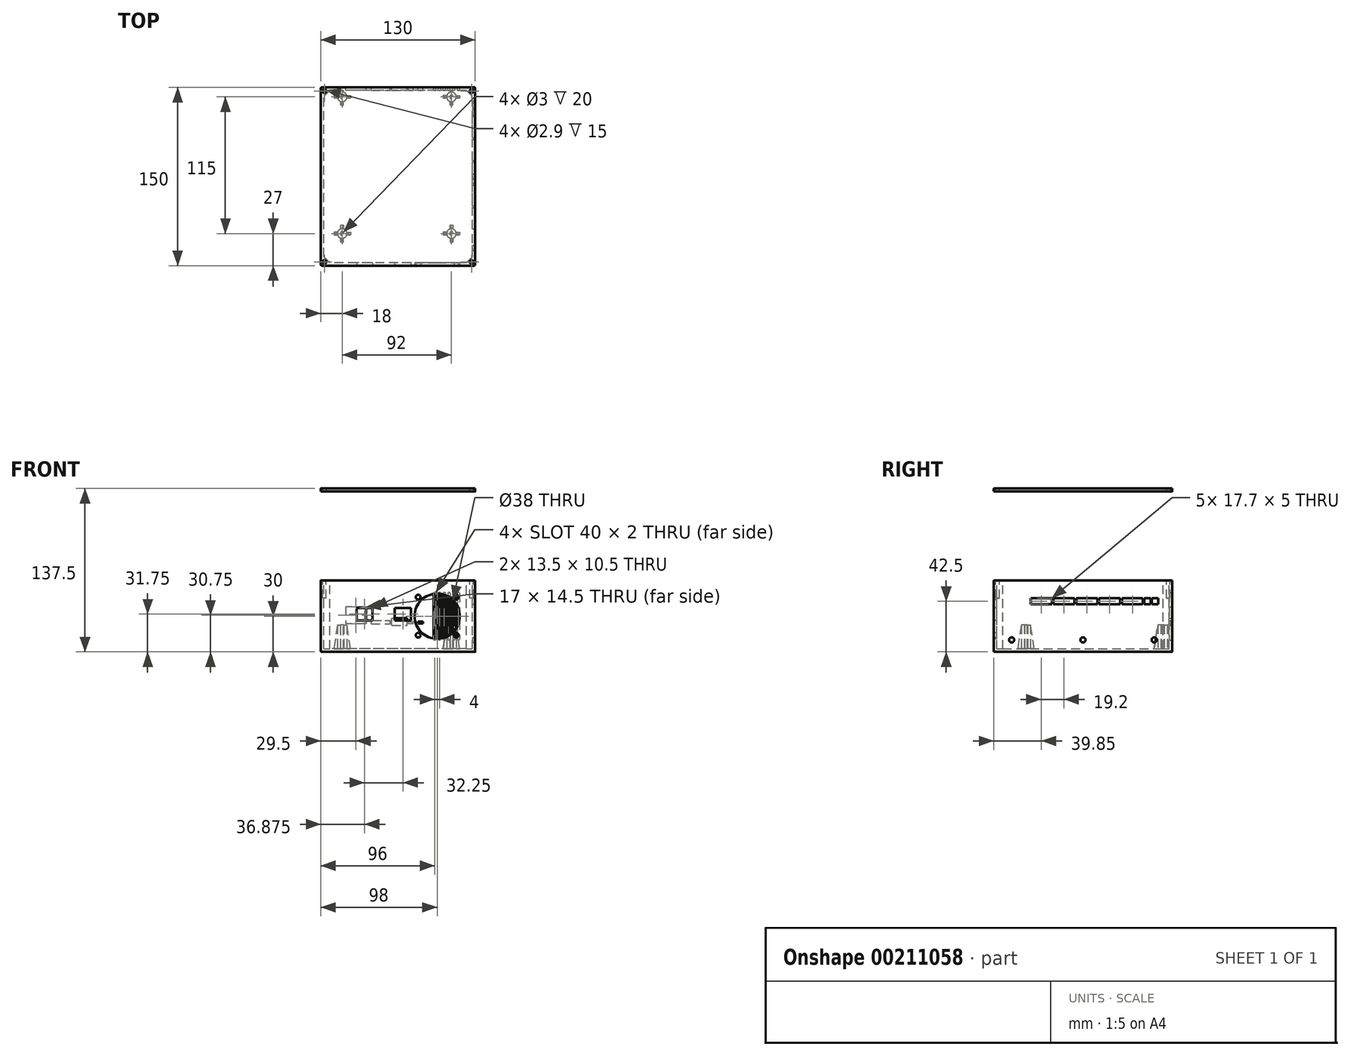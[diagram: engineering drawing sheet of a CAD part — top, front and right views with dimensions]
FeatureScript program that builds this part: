
annotation { "Feature Type Name" : "Feature", "Feature Type Description" : "" }
export const myFeature = defineFeature(function(context is Context, id is Id, definition is map)
    precondition{}
    {
        {
            var Q0;
            Q0=qCreatedBy(makeId("Top.planeOp"),FACE);
            var sketch = newSketch(context, id + "F0", { "sketchPlane" : qUnion([Q0])});
            skLineSegment(sketch, "E0.bottom", {"start": v(65, -75) * mm, "end": v(-65, -75) * mm});
            skLineSegment(sketch, "E0.top", {"start": v(65, 75) * mm, "end": v(-65, 75) * mm});
            skLineSegment(sketch, "E0.left", {"start": v(65, -75) * mm, "end": v(65, 75) * mm});
            skLineSegment(sketch, "E0.right", {"start": v(-65, -75) * mm, "end": v(-65, 75) * mm});
            skPoint(sketch, "E0.middle", {"position": v(0, 0) * mm});
            skCircle(sketch, "E1", {"center": v(-47, 67) * mm, "radius": 1.5 * mm});
            skCircle(sketch, "E2", {"center": v(45, 67) * mm, "radius": 1.5 * mm});
            skCircle(sketch, "E3", {"center": v(45, -48) * mm, "radius": 1.5 * mm});
            skCircle(sketch, "E4", {"center": v(-47, -48) * mm, "radius": 1.5 * mm});
            skCircle(sketch, "E5", {"center": v(-47, -48) * mm, "radius": 4 * mm});
            skCircle(sketch, "E6", {"center": v(45, -48) * mm, "radius": 4 * mm});
            skCircle(sketch, "E7", {"center": v(45, 67) * mm, "radius": 4 * mm});
            skCircle(sketch, "E8", {"center": v(-47, 67) * mm, "radius": 4 * mm});
            skLineSegment(sketch, "E9.bottom", {"start": v(46, 74) * mm, "end": v(44, 74) * mm});
            skLineSegment(sketch, "E9.top", {"start": v(46, 60) * mm, "end": v(44, 60) * mm});
            skLineSegment(sketch, "E9.left", {"start": v(46, 74) * mm, "end": v(46, 70.87) * mm});
            skLineSegment(sketch, "E9.right", {"start": v(44, 74) * mm, "end": v(44, 70.87) * mm});
            skLineSegment(sketch, "E10.bottom", {"start": v(52, 66) * mm, "end": v(48.87, 66) * mm});
            skLineSegment(sketch, "E10.top", {"start": v(52, 68) * mm, "end": v(48.87, 68) * mm});
            skLineSegment(sketch, "E10.left", {"start": v(52, 66) * mm, "end": v(52, 68) * mm});
            skLineSegment(sketch, "E10.right", {"start": v(38, 66) * mm, "end": v(38, 68) * mm});
            skLineSegment(sketch, "E11.trimOffspring", {"start": v(41.13, 68) * mm, "end": v(38, 68) * mm});
            skLineSegment(sketch, "E12.trimOffspring", {"start": v(41.13, 66) * mm, "end": v(38, 66) * mm});
            skLineSegment(sketch, "E13.trimOffspring", {"start": v(44, 63.13) * mm, "end": v(44, 60) * mm});
            skLineSegment(sketch, "E14.trimOffspring", {"start": v(46, 63.13) * mm, "end": v(46, 60) * mm});
            skLineSegment(sketch, "E15.bottom", {"start": v(-40, 66) * mm, "end": v(-43.13, 66) * mm});
            skLineSegment(sketch, "E15.top", {"start": v(-40, 68) * mm, "end": v(-43.13, 68) * mm});
            skLineSegment(sketch, "E15.left", {"start": v(-40, 66) * mm, "end": v(-40, 68) * mm});
            skLineSegment(sketch, "E15.right", {"start": v(-54, 66) * mm, "end": v(-54, 68) * mm});
            skLineSegment(sketch, "E16.bottom", {"start": v(-46, 74) * mm, "end": v(-48, 74) * mm});
            skLineSegment(sketch, "E16.top", {"start": v(-46, 60) * mm, "end": v(-48, 60) * mm});
            skLineSegment(sketch, "E16.left", {"start": v(-46, 74) * mm, "end": v(-46, 70.87) * mm});
            skLineSegment(sketch, "E16.right", {"start": v(-48, 74) * mm, "end": v(-48, 70.87) * mm});
            skLineSegment(sketch, "E17.trimOffspring", {"start": v(-50.87, 68) * mm, "end": v(-54, 68) * mm});
            skLineSegment(sketch, "E18.trimOffspring", {"start": v(-50.87, 66) * mm, "end": v(-54, 66) * mm});
            skLineSegment(sketch, "E19.trimOffspring", {"start": v(-48, 63.13) * mm, "end": v(-48, 60) * mm});
            skLineSegment(sketch, "E20.trimOffspring", {"start": v(-46, 63.13) * mm, "end": v(-46, 60) * mm});
            skLineSegment(sketch, "E21.bottom", {"start": v(-40, -49) * mm, "end": v(-43.13, -49) * mm});
            skLineSegment(sketch, "E21.top", {"start": v(-40, -47) * mm, "end": v(-43.13, -47) * mm});
            skLineSegment(sketch, "E21.left", {"start": v(-40, -49) * mm, "end": v(-40, -47) * mm});
            skLineSegment(sketch, "E21.right", {"start": v(-54, -49) * mm, "end": v(-54, -47) * mm});
            skLineSegment(sketch, "E22.bottom", {"start": v(-46, -41) * mm, "end": v(-48, -41) * mm});
            skLineSegment(sketch, "E22.top", {"start": v(-46, -55) * mm, "end": v(-48, -55) * mm});
            skLineSegment(sketch, "E22.left", {"start": v(-46, -41) * mm, "end": v(-46, -44.13) * mm});
            skLineSegment(sketch, "E22.right", {"start": v(-48, -41) * mm, "end": v(-48, -44.13) * mm});
            skLineSegment(sketch, "E23.trimOffspring", {"start": v(-50.87, -49) * mm, "end": v(-54, -49) * mm});
            skLineSegment(sketch, "E24.trimOffspring", {"start": v(-50.87, -47) * mm, "end": v(-54, -47) * mm});
            skLineSegment(sketch, "E25.trimOffspring", {"start": v(-46, -51.87) * mm, "end": v(-46, -55) * mm});
            skLineSegment(sketch, "E26.trimOffspring", {"start": v(-48, -51.87) * mm, "end": v(-48, -55) * mm});
            skLineSegment(sketch, "E27.bottom", {"start": v(52, -49) * mm, "end": v(48.87, -49) * mm});
            skLineSegment(sketch, "E27.top", {"start": v(52, -47) * mm, "end": v(48.87, -47) * mm});
            skLineSegment(sketch, "E27.left", {"start": v(52, -49) * mm, "end": v(52, -47) * mm});
            skLineSegment(sketch, "E27.right", {"start": v(38, -49) * mm, "end": v(38, -47) * mm});
            skLineSegment(sketch, "E28.bottom", {"start": v(46, -55) * mm, "end": v(44, -55) * mm});
            skLineSegment(sketch, "E28.top", {"start": v(46, -41) * mm, "end": v(44, -41) * mm});
            skLineSegment(sketch, "E28.left", {"start": v(46, -55) * mm, "end": v(46, -51.87) * mm});
            skLineSegment(sketch, "E28.right", {"start": v(44, -55) * mm, "end": v(44, -51.87) * mm});
            skLineSegment(sketch, "E29.trimOffspring", {"start": v(41.13, -49) * mm, "end": v(38, -49) * mm});
            skLineSegment(sketch, "E30.trimOffspring", {"start": v(41.13, -47) * mm, "end": v(38, -47) * mm});
            skLineSegment(sketch, "E31.trimOffspring", {"start": v(44, -44.13) * mm, "end": v(44, -41) * mm});
            skLineSegment(sketch, "E32.trimOffspring", {"start": v(46, -44.13) * mm, "end": v(46, -41) * mm});
            skLineSegment(sketch, "E33", {"start": v(65, 65) * mm, "end": v(55, 75) * mm});
            skLineSegment(sketch, "E34", {"start": v(65, -65) * mm, "end": v(55, -75) * mm});
            skLineSegment(sketch, "E35", {"start": v(-55, 75) * mm, "end": v(-65, 65) * mm});
            skLineSegment(sketch, "E36", {"start": v(-65, -65) * mm, "end": v(-55, -75) * mm});
            skSolve(sketch);
        }
        {
            var Q0;
            Q0=makeQuery(id+"F0.imprint","IMPRINT",FACE,{"disambiguationData":[TD([[makeQuery(id+"F0.imprint","IMPRINT",EDGE,{"derivedFrom":sQuery(id+"F0.wireOp",EDGE,"E0.bottom")}),-1.0]])]});
            var Q1;
            Q1=makeQuery(id+"F0.imprint","IMPRINT",FACE,{"disambiguationData":[TD([[makeQuery(id+"F0.imprint","IMPRINT",EDGE,{"derivedFrom":sQuery(id+"F0.wireOp",EDGE,"E2")}),-1.0]])]});
            var Q2;
            Q2=makeQuery(id+"F0.imprint","IMPRINT",FACE,{"disambiguationData":[TD([[makeQuery(id+"F0.imprint","IMPRINT",EDGE,{"derivedFrom":sQuery(id+"F0.wireOp",EDGE,"E4")}),-1.0]])]});
            var Q3;
            Q3=makeQuery(id+"F0.imprint","IMPRINT",FACE,{"disambiguationData":[TD([[makeQuery(id+"F0.imprint","IMPRINT",EDGE,{"derivedFrom":sQuery(id+"F0.wireOp",EDGE,"E16.top")}),-1.0]])]});
            var Q4;
            Q4=makeQuery(id+"F0.imprint","IMPRINT",FACE,{"disambiguationData":[TD([[makeQuery(id+"F0.imprint","IMPRINT",EDGE,{"derivedFrom":sQuery(id+"F0.wireOp",EDGE,"E21.right")}),-1.0]])]});
            var Q5;
            Q5=makeQuery(id+"F0.imprint","IMPRINT",FACE,{"disambiguationData":[TD([[makeQuery(id+"F0.imprint","IMPRINT",EDGE,{"derivedFrom":sQuery(id+"F0.wireOp",EDGE,"E22.top")}),-1.0]])]});
            var Q6;
            Q6=makeQuery(id+"F0.imprint","IMPRINT",FACE,{"disambiguationData":[TD([[makeQuery(id+"F0.imprint","IMPRINT",EDGE,{"derivedFrom":sQuery(id+"F0.wireOp",EDGE,"E1")}),-1.0]])]});
            var Q7;
            Q7=makeQuery(id+"F0.imprint","IMPRINT",FACE,{"disambiguationData":[TD([[makeQuery(id+"F0.imprint","IMPRINT",EDGE,{"derivedFrom":sQuery(id+"F0.wireOp",EDGE,"E3")}),-1.0]])]});
            var Q8;
            Q8=makeQuery(id+"F0.imprint","IMPRINT",FACE,{"disambiguationData":[TD([[makeQuery(id+"F0.imprint","IMPRINT",EDGE,{"derivedFrom":sQuery(id+"F0.wireOp",EDGE,"E15.right")}),-1.0]])]});
            var Q9;
            Q9=makeQuery(id+"F0.imprint","IMPRINT",FACE,{"disambiguationData":[TD([[makeQuery(id+"F0.imprint","IMPRINT",EDGE,{"derivedFrom":sQuery(id+"F0.wireOp",EDGE,"E28.bottom")}),-1.0]])]});
            var Q10;
            {var subQ0=sQuery(id+"F0.wireOp",EDGE,"E10.bottom");Q10=makeQuery(id+"F0.imprint","IMPRINT",FACE,{"disambiguationData":[TD([[makeQuery(id+"F0.imprint","IMPRINT",EDGE,{"derivedFrom":subQ0}),-1.0]])]});}
            var Q11;
            Q11=makeQuery(id+"F0.imprint","IMPRINT",FACE,{"disambiguationData":[TD([[makeQuery(id+"F0.imprint","IMPRINT",EDGE,{"derivedFrom":sQuery(id+"F0.wireOp",EDGE,"E9.top")}),-1.0]])]});
            var Q12;
            {var subQ0=sQuery(id+"F0.wireOp",EDGE,"E21.bottom");Q12=makeQuery(id+"F0.imprint","IMPRINT",FACE,{"disambiguationData":[TD([[makeQuery(id+"F0.imprint","IMPRINT",EDGE,{"derivedFrom":subQ0}),-1.0]])]});}
            var Q13;
            Q13=makeQuery(id+"F0.imprint","IMPRINT",FACE,{"disambiguationData":[TD([[makeQuery(id+"F0.imprint","IMPRINT",EDGE,{"derivedFrom":sQuery(id+"F0.wireOp",EDGE,"E28.top")}),1.0]])]});
            var Q14;
            Q14=makeQuery(id+"F0.imprint","IMPRINT",FACE,{"disambiguationData":[TD([[makeQuery(id+"F0.imprint","IMPRINT",EDGE,{"derivedFrom":sQuery(id+"F0.wireOp",EDGE,"E27.right")}),-1.0]])]});
            var Q15;
            Q15=makeQuery(id+"F0.imprint","IMPRINT",FACE,{"disambiguationData":[TD([[makeQuery(id+"F0.imprint","IMPRINT",EDGE,{"derivedFrom":sQuery(id+"F0.wireOp",EDGE,"E22.bottom")}),1.0]])]});
            var Q16;
            {var subQ0=sQuery(id+"F0.wireOp",EDGE,"E15.bottom");Q16=makeQuery(id+"F0.imprint","IMPRINT",FACE,{"disambiguationData":[TD([[makeQuery(id+"F0.imprint","IMPRINT",EDGE,{"derivedFrom":subQ0}),-1.0]])]});}
            var Q17;
            Q17=makeQuery(id+"F0.imprint","IMPRINT",FACE,{"disambiguationData":[TD([[makeQuery(id+"F0.imprint","IMPRINT",EDGE,{"derivedFrom":sQuery(id+"F0.wireOp",EDGE,"E9.bottom")}),1.0]])]});
            var Q18;
            {var subQ0=sQuery(id+"F0.wireOp",EDGE,"E27.bottom");Q18=makeQuery(id+"F0.imprint","IMPRINT",FACE,{"disambiguationData":[TD([[makeQuery(id+"F0.imprint","IMPRINT",EDGE,{"derivedFrom":subQ0}),-1.0]])]});}
            var Q19;
            Q19=makeQuery(id+"F0.imprint","IMPRINT",FACE,{"disambiguationData":[TD([[makeQuery(id+"F0.imprint","IMPRINT",EDGE,{"derivedFrom":sQuery(id+"F0.wireOp",EDGE,"E10.right")}),-1.0]])]});
            var Q20;
            Q20=makeQuery(id+"F0.imprint","IMPRINT",FACE,{"disambiguationData":[TD([[makeQuery(id+"F0.imprint","IMPRINT",EDGE,{"derivedFrom":sQuery(id+"F0.wireOp",EDGE,"E16.bottom")}),1.0]])]});
            var Q21;
            Q21=makeQuery(id+"F0.imprint","IMPRINT",FACE,{"disambiguationData":[TD([[makeQuery(id+"F0.imprint","IMPRINT",EDGE,{"derivedFrom":sQuery(id+"F0.wireOp",EDGE,"E2")}),1.0]])]});
            var Q22;
            Q22=makeQuery(id+"F0.imprint","IMPRINT",FACE,{"disambiguationData":[TD([[makeQuery(id+"F0.imprint","IMPRINT",EDGE,{"derivedFrom":sQuery(id+"F0.wireOp",EDGE,"E1")}),1.0]])]});
            var Q23;
            Q23=makeQuery(id+"F0.imprint","IMPRINT",FACE,{"disambiguationData":[TD([[makeQuery(id+"F0.imprint","IMPRINT",EDGE,{"derivedFrom":sQuery(id+"F0.wireOp",EDGE,"E4")}),1.0]])]});
            var Q24;
            Q24=makeQuery(id+"F0.imprint","IMPRINT",FACE,{"disambiguationData":[TD([[makeQuery(id+"F0.imprint","IMPRINT",EDGE,{"derivedFrom":sQuery(id+"F0.wireOp",EDGE,"E3")}),1.0]])]});
            var Q25;
            Q25=makeQuery(id+"F0.imprint","IMPRINT",FACE,{"disambiguationData":[TD([[makeQuery(id+"F0.imprint","IMPRINT",EDGE,{"derivedFrom":sQuery(id+"F0.wireOp",EDGE,"E9.bottom")}),-1.0]])]});
            var Q26;
            {var subQ3=sQuery(id+"F0.wireOp",EDGE,"E33");Q26=makeQuery(id+"F0.imprint","IMPRINT",FACE,{"disambiguationData":[TD([[makeQuery(id+"F0.imprint","IMPRINT",EDGE,{"derivedFrom":subQ3}),-1.0]])]});}
            var Q27;
            {var subQ3=sQuery(id+"F0.wireOp",EDGE,"E35");Q27=makeQuery(id+"F0.imprint","IMPRINT",FACE,{"disambiguationData":[TD([[makeQuery(id+"F0.imprint","IMPRINT",EDGE,{"derivedFrom":subQ3}),-1.0]])]});}
            extrude(context, id + "F1", {"entities" : qUnion([Q0, Q1, Q2, Q3, Q4, Q5, Q6, Q7, Q8, Q9, Q10, Q11, Q12, Q13, Q14, Q15, Q16, Q17, Q18, Q19, Q20, Q21, Q22, Q23, Q24, Q25, Q26, Q27]), "depth" : 60 * mm});
        }
        {
            var Q0;
            Q0=makeQuery(id+"F1.opExtrude","CAP_FACE",FACE,{"disambiguationData":[OSD([sQuery(id+"F0.wireOp",EDGE,"E0.bottom"),sQuery(id+"F0.wireOp",EDGE,"E0.top"),sQuery(id+"F0.wireOp",EDGE,"E0.left"),sQuery(id+"F0.wireOp",EDGE,"E0.right")])],"isStart":false});
            shell(context, id + "F2", {"entities" : qUnion([Q0]), "thickness" : 2.5 * mm});
        }
        {
            var Q0;
            Q0=makeQuery(id+"F0.imprint","IMPRINT",FACE,{"disambiguationData":[TD([[makeQuery(id+"F0.imprint","IMPRINT",EDGE,{"derivedFrom":sQuery(id+"F0.wireOp",EDGE,"E1")}),-1.0]])]});
            var Q1;
            Q1=makeQuery(id+"F0.imprint","IMPRINT",FACE,{"disambiguationData":[TD([[makeQuery(id+"F0.imprint","IMPRINT",EDGE,{"derivedFrom":sQuery(id+"F0.wireOp",EDGE,"E4")}),-1.0]])]});
            var Q2;
            Q2=makeQuery(id+"F0.imprint","IMPRINT",FACE,{"disambiguationData":[TD([[makeQuery(id+"F0.imprint","IMPRINT",EDGE,{"derivedFrom":sQuery(id+"F0.wireOp",EDGE,"E3")}),-1.0]])]});
            var Q3;
            Q3=makeQuery(id+"F0.imprint","IMPRINT",FACE,{"disambiguationData":[TD([[makeQuery(id+"F0.imprint","IMPRINT",EDGE,{"derivedFrom":sQuery(id+"F0.wireOp",EDGE,"E2")}),-1.0]])]});
            var Q4;
            {var subQ0=sQuery(id+"F0.wireOp",EDGE,"E10.bottom");Q4=makeQuery(id+"F0.imprint","IMPRINT",FACE,{"disambiguationData":[TD([[makeQuery(id+"F0.imprint","IMPRINT",EDGE,{"derivedFrom":subQ0}),-1.0]])]});}
            var Q5;
            Q5=makeQuery(id+"F0.imprint","IMPRINT",FACE,{"disambiguationData":[TD([[makeQuery(id+"F0.imprint","IMPRINT",EDGE,{"derivedFrom":sQuery(id+"F0.wireOp",EDGE,"E9.top")}),-1.0]])]});
            var Q6;
            Q6=makeQuery(id+"F0.imprint","IMPRINT",FACE,{"disambiguationData":[TD([[makeQuery(id+"F0.imprint","IMPRINT",EDGE,{"derivedFrom":sQuery(id+"F0.wireOp",EDGE,"E10.right")}),-1.0]])]});
            var Q7;
            Q7=makeQuery(id+"F0.imprint","IMPRINT",FACE,{"disambiguationData":[TD([[makeQuery(id+"F0.imprint","IMPRINT",EDGE,{"derivedFrom":sQuery(id+"F0.wireOp",EDGE,"E9.bottom")}),1.0]])]});
            var Q8;
            Q8=makeQuery(id+"F0.imprint","IMPRINT",FACE,{"disambiguationData":[TD([[makeQuery(id+"F0.imprint","IMPRINT",EDGE,{"derivedFrom":sQuery(id+"F0.wireOp",EDGE,"E16.bottom")}),1.0]])]});
            var Q9;
            Q9=makeQuery(id+"F0.imprint","IMPRINT",FACE,{"disambiguationData":[TD([[makeQuery(id+"F0.imprint","IMPRINT",EDGE,{"derivedFrom":sQuery(id+"F0.wireOp",EDGE,"E15.right")}),-1.0]])]});
            var Q10;
            Q10=makeQuery(id+"F0.imprint","IMPRINT",FACE,{"disambiguationData":[TD([[makeQuery(id+"F0.imprint","IMPRINT",EDGE,{"derivedFrom":sQuery(id+"F0.wireOp",EDGE,"E16.top")}),-1.0]])]});
            var Q11;
            {var subQ0=sQuery(id+"F0.wireOp",EDGE,"E15.bottom");Q11=makeQuery(id+"F0.imprint","IMPRINT",FACE,{"disambiguationData":[TD([[makeQuery(id+"F0.imprint","IMPRINT",EDGE,{"derivedFrom":subQ0}),-1.0]])]});}
            var Q12;
            {var subQ0=sQuery(id+"F0.wireOp",EDGE,"E21.bottom");Q12=makeQuery(id+"F0.imprint","IMPRINT",FACE,{"disambiguationData":[TD([[makeQuery(id+"F0.imprint","IMPRINT",EDGE,{"derivedFrom":subQ0}),-1.0]])]});}
            var Q13;
            Q13=makeQuery(id+"F0.imprint","IMPRINT",FACE,{"disambiguationData":[TD([[makeQuery(id+"F0.imprint","IMPRINT",EDGE,{"derivedFrom":sQuery(id+"F0.wireOp",EDGE,"E22.bottom")}),1.0]])]});
            var Q14;
            Q14=makeQuery(id+"F0.imprint","IMPRINT",FACE,{"disambiguationData":[TD([[makeQuery(id+"F0.imprint","IMPRINT",EDGE,{"derivedFrom":sQuery(id+"F0.wireOp",EDGE,"E21.right")}),-1.0]])]});
            var Q15;
            Q15=makeQuery(id+"F0.imprint","IMPRINT",FACE,{"disambiguationData":[TD([[makeQuery(id+"F0.imprint","IMPRINT",EDGE,{"derivedFrom":sQuery(id+"F0.wireOp",EDGE,"E22.top")}),-1.0]])]});
            var Q16;
            Q16=makeQuery(id+"F0.imprint","IMPRINT",FACE,{"disambiguationData":[TD([[makeQuery(id+"F0.imprint","IMPRINT",EDGE,{"derivedFrom":sQuery(id+"F0.wireOp",EDGE,"E27.right")}),-1.0]])]});
            var Q17;
            Q17=makeQuery(id+"F0.imprint","IMPRINT",FACE,{"disambiguationData":[TD([[makeQuery(id+"F0.imprint","IMPRINT",EDGE,{"derivedFrom":sQuery(id+"F0.wireOp",EDGE,"E28.top")}),1.0]])]});
            var Q18;
            {var subQ0=sQuery(id+"F0.wireOp",EDGE,"E27.bottom");Q18=makeQuery(id+"F0.imprint","IMPRINT",FACE,{"disambiguationData":[TD([[makeQuery(id+"F0.imprint","IMPRINT",EDGE,{"derivedFrom":subQ0}),-1.0]])]});}
            var Q19;
            Q19=makeQuery(id+"F0.imprint","IMPRINT",FACE,{"disambiguationData":[TD([[makeQuery(id+"F0.imprint","IMPRINT",EDGE,{"derivedFrom":sQuery(id+"F0.wireOp",EDGE,"E28.bottom")}),-1.0]])]});
            extrude(context, id + "F3", {"entities" : qUnion([Q0, Q1, Q2, Q3, Q4, Q5, Q6, Q7, Q8, Q9, Q10, Q11, Q12, Q13, Q14, Q15, Q16, Q17, Q18, Q19]), "operationType" : NewBodyOperationType.ADD, "depth" : (20 + 2.5) * mm});
        }
        {
            var Q0;
            Q0=makeQuery(id+"F1.opExtrude","SWEPT_FACE",FACE,{"disambiguationData":[OSD([sQuery(id+"F0.wireOp",EDGE,"E0.top")])]});
            var sketch = newSketch(context, id + "F4", { "sketchPlane" : qUnion([Q0])});
            skLineSegment(sketch, "E37.bottom", {"start": v(27, 38) * mm, "end": v(44, 38) * mm});
            skLineSegment(sketch, "E37.top", {"start": v(27, 23.5) * mm, "end": v(44, 23.5) * mm});
            skLineSegment(sketch, "E37.left", {"start": v(27, 38) * mm, "end": v(27, 23.5) * mm});
            skLineSegment(sketch, "E37.right", {"start": v(44, 38) * mm, "end": v(44, 23.5) * mm});
            skLineSegment(sketch, "E38.bottom", {"start": v(22.5, 23.5) * mm, "end": v(6.7, 23.5) * mm});
            skLineSegment(sketch, "E38.top", {"start": v(22.5, 26.5) * mm, "end": v(6.7, 26.5) * mm});
            skLineSegment(sketch, "E38.left", {"start": v(22.5, 23.5) * mm, "end": v(22.5, 26.5) * mm});
            skLineSegment(sketch, "E38.right", {"start": v(6.7, 23.5) * mm, "end": v(6.7, 26.5) * mm});
            skLineSegment(sketch, "E39.bottom", {"start": v(5.25, 22.4) * mm, "end": v(-7.75, 22.4) * mm});
            skLineSegment(sketch, "E39.top", {"start": v(5.25, 28.4) * mm, "end": v(-7.75, 28.4) * mm});
            skLineSegment(sketch, "E39.left", {"start": v(5.25, 22.4) * mm, "end": v(5.25, 28.4) * mm});
            skLineSegment(sketch, "E39.right", {"start": v(-7.75, 22.4) * mm, "end": v(-7.75, 28.4) * mm});
            skLineSegment(sketch, "E40.bottom", {"start": v(-8.65, 24) * mm, "end": v(-12.65, 24) * mm});
            skLineSegment(sketch, "E40.top", {"start": v(-8.65, 25.45) * mm, "end": v(-12.65, 25.45) * mm});
            skLineSegment(sketch, "E40.left", {"start": v(-8.65, 24) * mm, "end": v(-8.65, 25.45) * mm});
            skLineSegment(sketch, "E40.right", {"start": v(-12.65, 24) * mm, "end": v(-12.65, 25.45) * mm});
            skLineSegment(sketch, "E41.bottom", {"start": v(-16.95, 24) * mm, "end": v(-20.95, 24) * mm});
            skLineSegment(sketch, "E41.top", {"start": v(-16.95, 25.45) * mm, "end": v(-20.95, 25.45) * mm});
            skLineSegment(sketch, "E41.left", {"start": v(-16.95, 24) * mm, "end": v(-16.95, 25.45) * mm});
            skLineSegment(sketch, "E41.right", {"start": v(-20.95, 24) * mm, "end": v(-20.95, 25.45) * mm});
            skSolve(sketch);
        }
        {
            var Q0;
            Q0=qSketchRegion(id+"F4",true);
            extrude(context, id + "F5", {"entities" : qUnion([Q0]), "operationType" : NewBodyOperationType.REMOVE, "endBound" : BoundingType.UP_TO_NEXT, "oppositeDirection" : true, "depth" : 25 * mm});
        }
        {
            var Q0;
            Q0=makeQuery(id+"F1.opExtrude","SWEPT_FACE",FACE,{"disambiguationData":[OSD([sQuery(id+"F0.wireOp",EDGE,"E0.bottom")])]});
            var sketch = newSketch(context, id + "F6", { "sketchPlane" : qUnion([Q0])});
            skCircle(sketch, "E42", {"center": v(33, 30) * mm, "radius": 19 * mm});
            skPoint(sketch, "E42.centerSnap0", {"position": v(13, 30) * mm});
            skPoint(sketch, "E42.centerSnap1", {"position": v(33, 50) * mm});
            skCircle(sketch, "E43", {"center": v(17, 46) * mm, "radius": 2 * mm});
            skCircle(sketch, "E44", {"center": v(49, 46) * mm, "radius": 2 * mm});
            skCircle(sketch, "E45", {"center": v(49, 14) * mm, "radius": 2 * mm});
            skCircle(sketch, "E46", {"center": v(17, 14) * mm, "radius": 2 * mm});
            skLineSegment(sketch, "E47.bottom", {"start": v(17, 14) * mm, "end": v(49, 14) * mm, "construction": true});
            skLineSegment(sketch, "E47.top", {"start": v(17, 46) * mm, "end": v(49, 46) * mm, "construction": true});
            skLineSegment(sketch, "E47.left", {"start": v(17, 14) * mm, "end": v(17, 46) * mm, "construction": true});
            skLineSegment(sketch, "E47.right", {"start": v(49, 14) * mm, "end": v(49, 46) * mm, "construction": true});
            skLineSegment(sketch, "E48.bottom", {"start": v(-2.63, 37) * mm, "end": v(10.87, 37) * mm});
            skLineSegment(sketch, "E48.top", {"start": v(-2.63, 26.5) * mm, "end": v(10.87, 26.5) * mm});
            skLineSegment(sketch, "E48.left", {"start": v(-2.63, 37) * mm, "end": v(-2.63, 26.5) * mm});
            skLineSegment(sketch, "E48.right", {"start": v(10.87, 37) * mm, "end": v(10.87, 26.5) * mm});
            skLineSegment(sketch, "E49.bottom", {"start": v(-34.88, 37) * mm, "end": v(-21.38, 37) * mm});
            skLineSegment(sketch, "E49.top", {"start": v(-34.88, 26.5) * mm, "end": v(-21.38, 26.5) * mm});
            skLineSegment(sketch, "E49.left", {"start": v(-34.88, 37) * mm, "end": v(-34.88, 26.5) * mm});
            skLineSegment(sketch, "E49.right", {"start": v(-21.38, 37) * mm, "end": v(-21.38, 26.5) * mm});
            skSolve(sketch);
        }
        {
            var Q0;
            Q0=qSketchRegion(id+"F6",true);
            extrude(context, id + "F7", {"entities" : qUnion([Q0]), "operationType" : NewBodyOperationType.REMOVE, "endBound" : BoundingType.UP_TO_NEXT, "oppositeDirection" : true, "depth" : 25 * mm});
        }
        {
            var Q0;
            Q0=makeQuery(id+"F1.opExtrude","SWEPT_FACE",FACE,{"disambiguationData":[OSD([sQuery(id+"F0.wireOp",EDGE,"E0.left")])]});
            var sketch = newSketch(context, id + "F8", { "sketchPlane" : qUnion([Q0])});
            skLineSegment(sketch, "E50.bottom", {"start": v(-75, 0) * mm, "end": v(75, 0) * mm, "construction": true});
            skLineSegment(sketch, "E50.top", {"start": v(-75, 20) * mm, "end": v(75, 20) * mm, "construction": true});
            skLineSegment(sketch, "E50.left", {"start": v(-75, 0) * mm, "end": v(-75, 20) * mm, "construction": true});
            skLineSegment(sketch, "E50.right", {"start": v(75, 0) * mm, "end": v(75, 20) * mm, "construction": true});
            skCircle(sketch, "E51", {"center": v(-60, 10) * mm, "radius": 2.15 * mm});
            skPoint(sketch, "E51.centerSnap0", {"position": v(-75, 10) * mm});
            skCircle(sketch, "E52", {"center": v(60, 10) * mm, "radius": 2.15 * mm});
            skCircle(sketch, "E53", {"center": v(0, 10) * mm, "radius": 2.15 * mm});
            skPoint(sketch, "E53.centerSnap0", {"position": v(0, 0) * mm});
            skPoint(sketch, "E54.firstSnap0", {"position": v(-75, 40) * mm});
            skLineSegment(sketch, "E54.bottom", {"start": v(-44, 40) * mm, "end": v(-26.3, 40) * mm});
            skLineSegment(sketch, "E54.top", {"start": v(-44, 45) * mm, "end": v(-26.3, 45) * mm});
            skLineSegment(sketch, "E54.left", {"start": v(-44, 40) * mm, "end": v(-44, 45) * mm});
            skLineSegment(sketch, "E54.right", {"start": v(63.5, 40) * mm, "end": v(63.5, 45) * mm});
            skLineSegment(sketch, "E55.bottom", {"start": v(63.5, 45) * mm, "end": v(58, 45) * mm});
            skLineSegment(sketch, "E55.top", {"start": v(63.5, 40) * mm, "end": v(58, 40) * mm});
            skLineSegment(sketch, "E55.left", {"start": v(63.5, 45) * mm, "end": v(63.5, 40) * mm});
            skLineSegment(sketch, "E55.right", {"start": v(58, 45) * mm, "end": v(58, 40) * mm});
            skLineSegment(sketch, "E56.bottom", {"start": v(57, 45) * mm, "end": v(51.5, 45) * mm});
            skLineSegment(sketch, "E56.top", {"start": v(57, 40) * mm, "end": v(51.5, 40) * mm});
            skLineSegment(sketch, "E56.left", {"start": v(57, 45) * mm, "end": v(57, 40) * mm});
            skLineSegment(sketch, "E56.right", {"start": v(51.5, 45) * mm, "end": v(51.5, 40) * mm});
            skLineSegment(sketch, "E57.trimOffspring", {"start": v(58, 45) * mm, "end": v(63.5, 45) * mm});
            skLineSegment(sketch, "E58.trimOffspring", {"start": v(58, 40) * mm, "end": v(63.5, 40) * mm});
            skLineSegment(sketch, "E59", {"start": v(50.5, 45) * mm, "end": v(50.5, 40) * mm});
            skLineSegment(sketch, "E60.trimOffspring", {"start": v(51.5, 45) * mm, "end": v(57, 45) * mm});
            skLineSegment(sketch, "E61.trimOffspring", {"start": v(51.5, 40) * mm, "end": v(57, 40) * mm});
            skLineSegment(sketch, "E62.left", {"start": v(31.3, 45) * mm, "end": v(31.3, 40) * mm});
            skLineSegment(sketch, "E62.right", {"start": v(32.8, 45) * mm, "end": v(32.8, 40) * mm});
            skLineSegment(sketch, "E63.trimOffspring", {"start": v(32.8, 45) * mm, "end": v(50.5, 45) * mm});
            skLineSegment(sketch, "E64.trimOffspring", {"start": v(32.8, 40) * mm, "end": v(50.5, 40) * mm});
            skLineSegment(sketch, "E65.left", {"start": v(12.1, 45) * mm, "end": v(12.1, 40) * mm});
            skLineSegment(sketch, "E65.right", {"start": v(13.6, 45) * mm, "end": v(13.6, 40) * mm});
            skLineSegment(sketch, "E66.left", {"start": v(-7.1, 45) * mm, "end": v(-7.1, 40) * mm});
            skLineSegment(sketch, "E66.right", {"start": v(-5.6, 45) * mm, "end": v(-5.6, 40) * mm});
            skLineSegment(sketch, "E67.trimOffspring", {"start": v(-5.6, 45) * mm, "end": v(12.1, 45) * mm});
            skLineSegment(sketch, "E68.trimOffspring", {"start": v(-5.6, 40) * mm, "end": v(12.1, 40) * mm});
            skLineSegment(sketch, "E69.trimOffspring", {"start": v(13.6, 45) * mm, "end": v(31.3, 45) * mm});
            skLineSegment(sketch, "E70.trimOffspring", {"start": v(13.6, 40) * mm, "end": v(31.3, 40) * mm});
            skLineSegment(sketch, "E71.left", {"start": v(-26.3, 45) * mm, "end": v(-26.3, 40) * mm});
            skLineSegment(sketch, "E71.right", {"start": v(-24.8, 45) * mm, "end": v(-24.8, 40) * mm});
            skLineSegment(sketch, "E72.trimOffspring", {"start": v(-24.8, 45) * mm, "end": v(-7.1, 45) * mm});
            skLineSegment(sketch, "E73.trimOffspring", {"start": v(-24.8, 40) * mm, "end": v(-7.1, 40) * mm});
            skLineSegment(sketch, "E74", {"start": v(-44, 45) * mm, "end": v(12.1, 45) * mm, "construction": true});
            skLineSegment(sketch, "E75", {"start": v(12.1, 40) * mm, "end": v(-44, 40) * mm, "construction": true});
            skLineSegment(sketch, "E76", {"start": v(13.6, 40) * mm, "end": v(63.5, 40) * mm, "construction": true});
            skLineSegment(sketch, "E77", {"start": v(63.5, 45) * mm, "end": v(13.6, 45) * mm, "construction": true});
            skSolve(sketch);
        }
        {
            var Q0;
            Q0=qSketchRegion(id+"F8",true);
            extrude(context, id + "F9", {"entities" : qUnion([Q0]), "operationType" : NewBodyOperationType.REMOVE, "endBound" : BoundingType.UP_TO_NEXT, "oppositeDirection" : true, "depth" : 25 * mm});
        }
        {
            var Q0;
            {var subQ0=sQuery(id+"F0.wireOp",EDGE,"E0.right");var subQ1=sQuery(id+"F0.wireOp",EDGE,"E0.left");var subQ2=sQuery(id+"F0.wireOp",EDGE,"E0.top");var subQ3=sQuery(id+"F0.wireOp",EDGE,"E0.bottom");Q0=makeQuery(id+"F3.boolean.opBoolean","SPLIT",FACE,{"disambiguationData":[TD([makeQuery(id+"F2.opShell","OFFSET_FACE",FACE,{"disambiguationData":[OSD([subQ3])]})])],"derivedFrom":makeQuery(id+"F2.opShell","OFFSET_FACE",FACE,{"disambiguationData":[OSD([subQ3,subQ2,subQ1,subQ0])]})});}
            var sketch = newSketch(context, id + "F10", { "sketchPlane" : qUnion([Q0])});
            skArc(sketch, "E78", {"start": v(57.5, 17.5) * mm, "mid": v(45.78, 45.78) * mm, "end": v(17.5, 57.5) * mm});
            skArc(sketch, "E79.0", {"start": v(55.5, 17.5) * mm, "mid": v(44.37, 44.37) * mm, "end": v(17.5, 55.5) * mm});
            skLineSegment(sketch, "E80", {"start": v(17.5, 57.5) * mm, "end": v(17.5, 55.5) * mm});
            skLineSegment(sketch, "E81", {"start": v(55.5, 17.5) * mm, "end": v(57.5, 17.5) * mm});
            skSolve(sketch);
        }
        {
            var Q0;
            Q0=makeQuery(id+"F1.opExtrude","SWEPT_FACE",FACE,{"disambiguationData":[OSD([sQuery(id+"F0.wireOp",EDGE,"E0.top")])]});
            var sketch = newSketch(context, id + "F11", { "sketchPlane" : qUnion([Q0])});
            skLineSegment(sketch, "E82.bottom", {"start": v(-51, 50) * mm, "end": v(-51, 50) * mm});
            skLineSegment(sketch, "E82.top", {"start": v(-51, 10) * mm, "end": v(-51, 10) * mm});
            skLineSegment(sketch, "E82.left", {"start": v(-52, 49) * mm, "end": v(-52, 11) * mm});
            skLineSegment(sketch, "E82.right", {"start": v(-50, 49) * mm, "end": v(-50, 11) * mm});
            skPoint(sketch, "E83.visualSharp", {"position": v(-52, 50) * mm});
            skArc(sketch, "E83.filletArc", {"start": v(-51, 50) * mm, "mid": v(-51.7, 49.7) * mm, "end": v(-52, 49) * mm});
            skArc(sketch, "E84.filletArc", {"start": v(-50, 49) * mm, "mid": v(-50.3, 49.7) * mm, "end": v(-51, 50) * mm});
            skPoint(sketch, "E85.visualSharp", {"position": v(-52, 10) * mm});
            skArc(sketch, "E85.filletArc", {"start": v(-52, 11) * mm, "mid": v(-51.7, 10.3) * mm, "end": v(-51, 10) * mm});
            skPoint(sketch, "E86.visualSharp", {"position": v(-50, 10) * mm});
            skArc(sketch, "E86.filletArc", {"start": v(-51, 10) * mm, "mid": v(-50.3, 10.3) * mm, "end": v(-50, 11) * mm});
            skPoint(sketch, "E87.1.0.0", {"position": v(-46, 10) * mm});
            skPoint(sketch, "E87.1.0.1", {"position": v(-48, 10) * mm});
            skPoint(sketch, "E87.1.0.2", {"position": v(-48, 50) * mm});
            skLineSegment(sketch, "E87.1.0.3", {"start": v(-48, 49) * mm, "end": v(-48, 11) * mm});
            skLineSegment(sketch, "E87.1.0.4", {"start": v(-46, 49) * mm, "end": v(-46, 11) * mm});
            skArc(sketch, "E87.1.0.5", {"start": v(-46, 49) * mm, "mid": v(-46.3, 49.7) * mm, "end": v(-47, 50) * mm});
            skArc(sketch, "E87.1.0.6", {"start": v(-47, 10) * mm, "mid": v(-46.3, 10.3) * mm, "end": v(-46, 11) * mm});
            skArc(sketch, "E87.1.0.7", {"start": v(-48, 11) * mm, "mid": v(-47.7, 10.3) * mm, "end": v(-47, 10) * mm});
            skArc(sketch, "E87.1.0.8", {"start": v(-47, 50) * mm, "mid": v(-47.7, 49.7) * mm, "end": v(-48, 49) * mm});
            skPoint(sketch, "E87.2.0.0", {"position": v(-42, 10) * mm});
            skPoint(sketch, "E87.2.0.1", {"position": v(-44, 10) * mm});
            skPoint(sketch, "E87.2.0.2", {"position": v(-44, 50) * mm});
            skLineSegment(sketch, "E87.2.0.3", {"start": v(-44, 49) * mm, "end": v(-44, 11) * mm});
            skLineSegment(sketch, "E87.2.0.4", {"start": v(-42, 49) * mm, "end": v(-42, 11) * mm});
            skArc(sketch, "E87.2.0.5", {"start": v(-42, 49) * mm, "mid": v(-42.3, 49.7) * mm, "end": v(-43, 50) * mm});
            skArc(sketch, "E87.2.0.6", {"start": v(-43, 10) * mm, "mid": v(-42.3, 10.3) * mm, "end": v(-42, 11) * mm});
            skArc(sketch, "E87.2.0.7", {"start": v(-44, 11) * mm, "mid": v(-43.7, 10.3) * mm, "end": v(-43, 10) * mm});
            skArc(sketch, "E87.2.0.8", {"start": v(-43, 50) * mm, "mid": v(-43.7, 49.7) * mm, "end": v(-44, 49) * mm});
            skPoint(sketch, "E87.3.0.0", {"position": v(-38, 10) * mm});
            skPoint(sketch, "E87.3.0.1", {"position": v(-40, 10) * mm});
            skPoint(sketch, "E87.3.0.2", {"position": v(-40, 50) * mm});
            skLineSegment(sketch, "E87.3.0.3", {"start": v(-40, 49) * mm, "end": v(-40, 11) * mm});
            skLineSegment(sketch, "E87.3.0.4", {"start": v(-38, 49) * mm, "end": v(-38, 11) * mm});
            skArc(sketch, "E87.3.0.5", {"start": v(-38, 49) * mm, "mid": v(-38.3, 49.7) * mm, "end": v(-39, 50) * mm});
            skArc(sketch, "E87.3.0.6", {"start": v(-39, 10) * mm, "mid": v(-38.3, 10.3) * mm, "end": v(-38, 11) * mm});
            skArc(sketch, "E87.3.0.7", {"start": v(-40, 11) * mm, "mid": v(-39.7, 10.3) * mm, "end": v(-39, 10) * mm});
            skArc(sketch, "E87.3.0.8", {"start": v(-39, 50) * mm, "mid": v(-39.7, 49.7) * mm, "end": v(-40, 49) * mm});
            skPoint(sketch, "E87.4.0.0", {"position": v(-34, 10) * mm});
            skPoint(sketch, "E87.4.0.1", {"position": v(-36, 10) * mm});
            skPoint(sketch, "E87.4.0.2", {"position": v(-36, 50) * mm});
            skLineSegment(sketch, "E87.4.0.3", {"start": v(-36, 49) * mm, "end": v(-36, 11) * mm});
            skLineSegment(sketch, "E87.4.0.4", {"start": v(-34, 49) * mm, "end": v(-34, 11) * mm});
            skArc(sketch, "E87.4.0.5", {"start": v(-34, 49) * mm, "mid": v(-34.3, 49.7) * mm, "end": v(-35, 50) * mm});
            skArc(sketch, "E87.4.0.6", {"start": v(-35, 10) * mm, "mid": v(-34.3, 10.3) * mm, "end": v(-34, 11) * mm});
            skArc(sketch, "E87.4.0.7", {"start": v(-36, 11) * mm, "mid": v(-35.7, 10.3) * mm, "end": v(-35, 10) * mm});
            skArc(sketch, "E87.4.0.8", {"start": v(-35, 50) * mm, "mid": v(-35.7, 49.7) * mm, "end": v(-36, 49) * mm});
            skPoint(sketch, "E87.5.0.0", {"position": v(-30, 10) * mm});
            skPoint(sketch, "E87.5.0.1", {"position": v(-32, 10) * mm});
            skPoint(sketch, "E87.5.0.2", {"position": v(-32, 50) * mm});
            skLineSegment(sketch, "E87.5.0.3", {"start": v(-32, 49) * mm, "end": v(-32, 11) * mm});
            skLineSegment(sketch, "E87.5.0.4", {"start": v(-30, 49) * mm, "end": v(-30, 11) * mm});
            skArc(sketch, "E87.5.0.5", {"start": v(-30, 49) * mm, "mid": v(-30.3, 49.7) * mm, "end": v(-31, 50) * mm});
            skArc(sketch, "E87.5.0.6", {"start": v(-31, 10) * mm, "mid": v(-30.3, 10.3) * mm, "end": v(-30, 11) * mm});
            skArc(sketch, "E87.5.0.7", {"start": v(-32, 11) * mm, "mid": v(-31.7, 10.3) * mm, "end": v(-31, 10) * mm});
            skArc(sketch, "E87.5.0.8", {"start": v(-31, 50) * mm, "mid": v(-31.7, 49.7) * mm, "end": v(-32, 49) * mm});
            skLineSegment(sketch, "E87.direction1", {"start": v(-52, 10) * mm, "end": v(-48, 10) * mm, "construction": true});
            skSolve(sketch);
        }
        {
            var Q0;
            Q0=qSketchRegion(id+"F11",true);
            extrude(context, id + "F12", {"entities" : qUnion([Q0]), "operationType" : NewBodyOperationType.REMOVE, "endBound" : BoundingType.UP_TO_NEXT, "oppositeDirection" : true, "depth" : 25 * mm});
        }
        {
            var Q0;
            Q0=makeQuery(id+"F3.opExtrude","CAP_EDGE",EDGE,{"disambiguationData":[OSD([sQuery(id+"F0.wireOp",EDGE,"E21.left")])],"isStart":false});
            var Q1;
            Q1=makeQuery(id+"F3.opExtrude","CAP_EDGE",EDGE,{"disambiguationData":[OSD([sQuery(id+"F0.wireOp",EDGE,"E22.bottom")])],"isStart":false});
            var Q2;
            Q2=makeQuery(id+"F3.opExtrude","CAP_EDGE",EDGE,{"disambiguationData":[OSD([sQuery(id+"F0.wireOp",EDGE,"E21.right")])],"isStart":false});
            var Q3;
            Q3=makeQuery(id+"F3.opExtrude","CAP_EDGE",EDGE,{"disambiguationData":[OSD([sQuery(id+"F0.wireOp",EDGE,"E22.top")])],"isStart":false});
            chamfer(context, id + "F13", {"entities" : qUnion([Q0, Q1, Q2, Q3]), "chamferType" : ChamferType.TWO_OFFSETS, "width1" : 3 * mm, "oppositeDirection" : false, "width2" : 20 * mm, "tangentPropagation" : true});
        }
        {
            var Q0;
            Q0=makeQuery(id+"F3.opExtrude","CAP_EDGE",EDGE,{"disambiguationData":[OSD([sQuery(id+"F0.wireOp",EDGE,"E16.top")])],"isStart":false});
            var Q1;
            Q1=makeQuery(id+"F3.opExtrude","CAP_EDGE",EDGE,{"disambiguationData":[OSD([sQuery(id+"F0.wireOp",EDGE,"E15.left")])],"isStart":false});
            var Q2;
            Q2=makeQuery(id+"F3.opExtrude","CAP_EDGE",EDGE,{"disambiguationData":[OSD([sQuery(id+"F0.wireOp",EDGE,"E15.right")])],"isStart":false});
            var Q3;
            Q3=makeQuery(id+"F3.opExtrude","CAP_EDGE",EDGE,{"disambiguationData":[OSD([sQuery(id+"F0.wireOp",EDGE,"E9.top")])],"isStart":false});
            var Q4;
            Q4=makeQuery(id+"F3.opExtrude","CAP_EDGE",EDGE,{"disambiguationData":[OSD([sQuery(id+"F0.wireOp",EDGE,"E10.right")])],"isStart":false});
            var Q5;
            Q5=makeQuery(id+"F3.opExtrude","CAP_EDGE",EDGE,{"disambiguationData":[OSD([sQuery(id+"F0.wireOp",EDGE,"E27.right")])],"isStart":false});
            var Q6;
            Q6=makeQuery(id+"F3.opExtrude","CAP_EDGE",EDGE,{"disambiguationData":[OSD([sQuery(id+"F0.wireOp",EDGE,"E28.bottom")])],"isStart":false});
            chamfer(context, id + "F14", {"entities" : qUnion([Q0, Q1, Q2, Q3, Q4, Q5, Q6]), "chamferType" : ChamferType.TWO_OFFSETS, "width1" : 20 * mm, "oppositeDirection" : false, "width2" : 3 * mm, "tangentPropagation" : true});
        }
        {
            var Q0;
            Q0=makeQuery(id+"F3.opExtrude","CAP_EDGE",EDGE,{"disambiguationData":[OSD([sQuery(id+"F0.wireOp",EDGE,"E27.left")])],"isStart":false});
            var Q1;
            Q1=makeQuery(id+"F3.opExtrude","CAP_EDGE",EDGE,{"disambiguationData":[OSD([sQuery(id+"F0.wireOp",EDGE,"E28.top")])],"isStart":false});
            var Q2;
            Q2=makeQuery(id+"F3.opExtrude","CAP_EDGE",EDGE,{"disambiguationData":[OSD([sQuery(id+"F0.wireOp",EDGE,"E10.left")])],"isStart":false});
            chamfer(context, id + "F15", {"entities" : qUnion([Q0, Q1, Q2]), "chamferType" : ChamferType.TWO_OFFSETS, "width1" : 3 * mm, "oppositeDirection" : false, "width2" : 20 * mm, "tangentPropagation" : true});
        }
        {
            var Q0;
            {var subQ3=sQuery(id+"F0.wireOp",EDGE,"E35");Q0=makeQuery(id+"F0.imprint","IMPRINT",FACE,{"disambiguationData":[TD([[makeQuery(id+"F0.imprint","IMPRINT",EDGE,{"derivedFrom":subQ3}),-1.0]])]});}
            var Q1;
            {var subQ3=sQuery(id+"F0.wireOp",EDGE,"E36");Q1=makeQuery(id+"F0.imprint","IMPRINT",FACE,{"disambiguationData":[TD([[makeQuery(id+"F0.imprint","IMPRINT",EDGE,{"derivedFrom":subQ3}),-1.0]])]});}
            var Q2;
            {var subQ3=sQuery(id+"F0.wireOp",EDGE,"E34");Q2=makeQuery(id+"F0.imprint","IMPRINT",FACE,{"disambiguationData":[TD([[makeQuery(id+"F0.imprint","IMPRINT",EDGE,{"derivedFrom":subQ3}),1.0]])]});}
            var Q3;
            {var subQ3=sQuery(id+"F0.wireOp",EDGE,"E33");Q3=makeQuery(id+"F0.imprint","IMPRINT",FACE,{"disambiguationData":[TD([[makeQuery(id+"F0.imprint","IMPRINT",EDGE,{"derivedFrom":subQ3}),-1.0]])]});}
            var Q4;
            Q4=makeQuery(id+"F1.opExtrude","CAP_FACE",FACE,{"disambiguationData":[OSD([sQuery(id+"F0.wireOp",EDGE,"E0.bottom"),sQuery(id+"F0.wireOp",EDGE,"E0.top"),sQuery(id+"F0.wireOp",EDGE,"E0.left"),sQuery(id+"F0.wireOp",EDGE,"E0.right")])],"isStart":false});
            extrude(context, id + "F16", {"entities" : qUnion([Q0, Q1, Q2, Q3]), "operationType" : NewBodyOperationType.ADD, "endBound" : BoundingType.UP_TO_SURFACE, "endBoundEntityFace" : qUnion([Q4]), "depth" : 25 * mm});
        }
        {
            var Q0;
            {var subQ0=sQuery(id+"F0.wireOp",EDGE,"E0.right");var subQ1=sQuery(id+"F0.wireOp",EDGE,"E0.top");var subQ2=sQuery(id+"F0.wireOp",EDGE,"E0.left");var subQ3=sQuery(id+"F0.wireOp",EDGE,"E0.bottom");Q0=makeQuery(id+"F16.boolean.opBoolean","MERGE",FACE,{"derivedFrom":[makeQuery(id+"F1.opExtrude","CAP_FACE",FACE,{"disambiguationData":[OSD([subQ3,subQ1,subQ2,subQ0])],"isStart":false}),makeQuery(id+"F16.opExtrude","CAP_FACE",FACE,{"disambiguationData":[OSD([subQ3,subQ1,subQ2,subQ0]),ownerDisambiguation([makeQuery(id+"F16.opExtrude","SWEPT_BODY",BODY,{"disambiguationData":[OSD([subQ3,subQ2,sQuery(id+"F0.wireOp",EDGE,"E34")])]})])],"isStart":false}),makeQuery(id+"F16.opExtrude","CAP_FACE",FACE,{"disambiguationData":[OSD([subQ3,subQ1,subQ2,subQ0]),ownerDisambiguation([makeQuery(id+"F16.opExtrude","SWEPT_BODY",BODY,{"disambiguationData":[OSD([subQ3,subQ0,sQuery(id+"F0.wireOp",EDGE,"E36")])]})])],"isStart":false}),makeQuery(id+"F16.opExtrude","CAP_FACE",FACE,{"disambiguationData":[OSD([subQ3,subQ1,subQ2,subQ0]),ownerDisambiguation([makeQuery(id+"F16.opExtrude","SWEPT_BODY",BODY,{"disambiguationData":[OSD([subQ1,subQ2,sQuery(id+"F0.wireOp",EDGE,"E33")])]})])],"isStart":false}),makeQuery(id+"F16.opExtrude","CAP_FACE",FACE,{"disambiguationData":[OSD([subQ3,subQ1,subQ2,subQ0]),ownerDisambiguation([makeQuery(id+"F16.opExtrude","SWEPT_BODY",BODY,{"disambiguationData":[OSD([subQ1,subQ0,sQuery(id+"F0.wireOp",EDGE,"E35")])]})])],"isStart":false})]});}
            var sketch = newSketch(context, id + "F17", { "sketchPlane" : qUnion([Q0])});
            skCircle(sketch, "E88", {"center": v(-61.9, -71.9) * mm, "radius": 1.45 * mm});
            skCircle(sketch, "E89", {"center": v(-61.9, 71.9) * mm, "radius": 1.45 * mm});
            skCircle(sketch, "E90", {"center": v(61.9, -71.9) * mm, "radius": 1.45 * mm});
            skCircle(sketch, "E91", {"center": v(61.9, 71.9) * mm, "radius": 1.45 * mm});
            skSolve(sketch);
        }
        {
            var Q0;
            Q0=qSketchRegion(id+"F17",true);
            extrude(context, id + "F18", {"entities" : qUnion([Q0]), "operationType" : NewBodyOperationType.REMOVE, "oppositeDirection" : true, "depth" : 15 * mm});
        }
        {
            var Q0;
            {var subQ0=sQuery(id+"F0.wireOp",EDGE,"E0.right");var subQ1=sQuery(id+"F0.wireOp",EDGE,"E0.top");var subQ2=sQuery(id+"F0.wireOp",EDGE,"E0.left");var subQ3=sQuery(id+"F0.wireOp",EDGE,"E0.bottom");Q0=makeQuery(id+"F16.boolean.opBoolean","MERGE",FACE,{"derivedFrom":[makeQuery(id+"F1.opExtrude","CAP_FACE",FACE,{"disambiguationData":[OSD([subQ3,subQ1,subQ2,subQ0])],"isStart":false}),makeQuery(id+"F16.opExtrude","CAP_FACE",FACE,{"disambiguationData":[OSD([subQ3,subQ1,subQ2,subQ0]),ownerDisambiguation([makeQuery(id+"F16.opExtrude","SWEPT_BODY",BODY,{"disambiguationData":[OSD([subQ3,subQ2,sQuery(id+"F0.wireOp",EDGE,"E34")])]})])],"isStart":false}),makeQuery(id+"F16.opExtrude","CAP_FACE",FACE,{"disambiguationData":[OSD([subQ3,subQ1,subQ2,subQ0]),ownerDisambiguation([makeQuery(id+"F16.opExtrude","SWEPT_BODY",BODY,{"disambiguationData":[OSD([subQ3,subQ0,sQuery(id+"F0.wireOp",EDGE,"E36")])]})])],"isStart":false}),makeQuery(id+"F16.opExtrude","CAP_FACE",FACE,{"disambiguationData":[OSD([subQ3,subQ1,subQ2,subQ0]),ownerDisambiguation([makeQuery(id+"F16.opExtrude","SWEPT_BODY",BODY,{"disambiguationData":[OSD([subQ1,subQ2,sQuery(id+"F0.wireOp",EDGE,"E33")])]})])],"isStart":false}),makeQuery(id+"F16.opExtrude","CAP_FACE",FACE,{"disambiguationData":[OSD([subQ3,subQ1,subQ2,subQ0]),ownerDisambiguation([makeQuery(id+"F16.opExtrude","SWEPT_BODY",BODY,{"disambiguationData":[OSD([subQ1,subQ0,sQuery(id+"F0.wireOp",EDGE,"E35")])]})])],"isStart":false})]});}
            var sketch = newSketch(context, id + "F19", { "sketchPlane" : qUnion([Q0])});
            skLineSegment(sketch, "E92.bottom", {"start": v(-65, 75) * mm, "end": v(65, 75) * mm});
            skLineSegment(sketch, "E92.top", {"start": v(-65, -75) * mm, "end": v(65, -75) * mm});
            skLineSegment(sketch, "E92.left", {"start": v(-65, 75) * mm, "end": v(-65, -75) * mm});
            skLineSegment(sketch, "E92.right", {"start": v(65, 75) * mm, "end": v(65, -75) * mm});
            skSolve(sketch);
        }
        {
            var Q0;
            Q0=qSketchRegion(id+"F19",true);
            extrude(context, id + "F20", {"entities" : qUnion([Q0]), "depth" : 2.5 * mm});
        }
        {
            var Q0;
            Q0=makeQuery(id+"F20.opExtrude","SWEPT_BODY",BODY,{"disambiguationData":[OSD([sQuery(id+"F19.wireOp",EDGE,"E92.bottom"),sQuery(id+"F19.wireOp",EDGE,"E92.top"),sQuery(id+"F19.wireOp",EDGE,"E92.left"),sQuery(id+"F19.wireOp",EDGE,"E92.right")])]});
            transform(context, id + "F21", {"entities" : qUnion([Q0]), "transformType" : TransformType.TRANSLATION_3D, "dx" : 0 * mm, "dy" : 0 * mm, "dz" : 75 * mm, "makeCopy" : false});
        }
        {
            var Q0;
            Q0=makeQuery(id+"F20.opExtrude","CAP_FACE",FACE,{"disambiguationData":[OSD([sQuery(id+"F19.wireOp",EDGE,"E92.bottom"),sQuery(id+"F19.wireOp",EDGE,"E92.top"),sQuery(id+"F19.wireOp",EDGE,"E92.left"),sQuery(id+"F19.wireOp",EDGE,"E92.right")])],"isStart":false});
            var sketch = newSketch(context, id + "F22", { "sketchPlane" : qUnion([Q0])});
            skCircle(sketch, "E93", {"center": v(61.9, -71.9) * mm, "radius": 1.6 * mm});
            skCircle(sketch, "E94", {"center": v(-61.9, -71.9) * mm, "radius": 1.6 * mm});
            skCircle(sketch, "E95", {"center": v(-61.9, 71.9) * mm, "radius": 1.6 * mm});
            skCircle(sketch, "E96", {"center": v(61.9, 71.9) * mm, "radius": 1.6 * mm});
            skCircle(sketch, "E97", {"center": v(-61.9, -71.9) * mm, "radius": 2.75 * mm});
            skCircle(sketch, "E98", {"center": v(61.9, -71.9) * mm, "radius": 2.75 * mm});
            skCircle(sketch, "E99", {"center": v(61.9, 71.9) * mm, "radius": 2.75 * mm});
            skCircle(sketch, "E100", {"center": v(-61.9, 71.9) * mm, "radius": 2.75 * mm});
            skSolve(sketch);
        }
        {
            var Q0;
            Q0=makeQuery(id+"F22.imprint","IMPRINT",FACE,{"disambiguationData":[TD([[makeQuery(id+"F22.imprint","IMPRINT",EDGE,{"derivedFrom":sQuery(id+"F22.wireOp",EDGE,"E94")}),1.0]])]});
            var Q1;
            Q1=makeQuery(id+"F22.imprint","IMPRINT",FACE,{"disambiguationData":[TD([[makeQuery(id+"F22.imprint","IMPRINT",EDGE,{"derivedFrom":sQuery(id+"F22.wireOp",EDGE,"E93")}),1.0]])]});
            var Q2;
            Q2=makeQuery(id+"F22.imprint","IMPRINT",FACE,{"disambiguationData":[TD([[makeQuery(id+"F22.imprint","IMPRINT",EDGE,{"derivedFrom":sQuery(id+"F22.wireOp",EDGE,"E96")}),1.0]])]});
            var Q3;
            Q3=makeQuery(id+"F22.imprint","IMPRINT",FACE,{"disambiguationData":[TD([[makeQuery(id+"F22.imprint","IMPRINT",EDGE,{"derivedFrom":sQuery(id+"F22.wireOp",EDGE,"E95")}),1.0]])]});
            extrude(context, id + "F23", {"entities" : qUnion([Q0, Q1, Q2, Q3]), "operationType" : NewBodyOperationType.REMOVE, "endBound" : BoundingType.UP_TO_NEXT, "oppositeDirection" : true, "depth" : 25 * mm});
        }
        {
            var Q0;
            Q0=makeQuery(id+"F1.opExtrude","SWEPT_EDGE",EDGE,{"disambiguationData":[OSD([sQuery(id+"F0.wireOp",EDGE,"E0.bottom"),sQuery(id+"F0.wireOp",EDGE,"E0.left")])]});
            var Q1;
            Q1=makeQuery(id+"F1.opExtrude","SWEPT_EDGE",EDGE,{"disambiguationData":[OSD([sQuery(id+"F0.wireOp",EDGE,"E0.bottom"),sQuery(id+"F0.wireOp",EDGE,"E0.right")])]});
            var Q2;
            Q2=makeQuery(id+"F1.opExtrude","SWEPT_EDGE",EDGE,{"disambiguationData":[OSD([sQuery(id+"F0.wireOp",EDGE,"E0.top"),sQuery(id+"F0.wireOp",EDGE,"E0.left")])]});
            var Q3;
            Q3=makeQuery(id+"F1.opExtrude","SWEPT_EDGE",EDGE,{"disambiguationData":[OSD([sQuery(id+"F0.wireOp",EDGE,"E0.top"),sQuery(id+"F0.wireOp",EDGE,"E0.right")])]});
            var Q4;
            Q4=makeQuery(id+"F1.opExtrude","CAP_EDGE",EDGE,{"disambiguationData":[OSD([sQuery(id+"F0.wireOp",EDGE,"E0.right")])],"isStart":true});
            var Q5;
            Q5=makeQuery(id+"F20.opExtrude","SWEPT_EDGE",EDGE,{"disambiguationData":[OSD([sQuery(id+"F19.wireOp",EDGE,"E92.top"),sQuery(id+"F19.wireOp",EDGE,"E92.right")])]});
            var Q6;
            Q6=makeQuery(id+"F20.opExtrude","SWEPT_EDGE",EDGE,{"disambiguationData":[OSD([sQuery(id+"F19.wireOp",EDGE,"E92.bottom"),sQuery(id+"F19.wireOp",EDGE,"E92.right")])]});
            var Q7;
            Q7=makeQuery(id+"F20.opExtrude","SWEPT_EDGE",EDGE,{"disambiguationData":[OSD([sQuery(id+"F19.wireOp",EDGE,"E92.bottom"),sQuery(id+"F19.wireOp",EDGE,"E92.left")])]});
            var Q8;
            Q8=makeQuery(id+"F20.opExtrude","SWEPT_EDGE",EDGE,{"disambiguationData":[OSD([sQuery(id+"F19.wireOp",EDGE,"E92.top"),sQuery(id+"F19.wireOp",EDGE,"E92.left")])]});
            fillet(context, id + "F24", {"entities" : qUnion([Q0, Q1, Q2, Q3, Q4, Q5, Q6, Q7, Q8]), "radius" : 1 * mm, "tangentPropagation" : true, "allowEdgeOverflow" : false});
        }
    });
